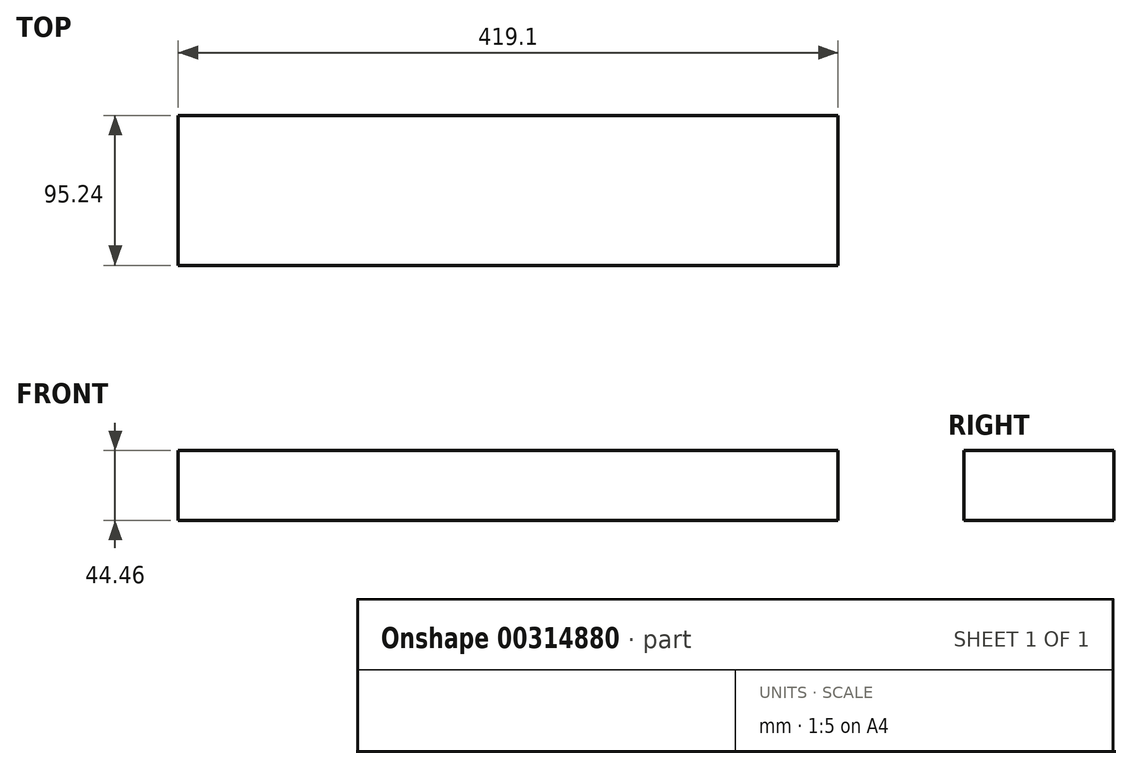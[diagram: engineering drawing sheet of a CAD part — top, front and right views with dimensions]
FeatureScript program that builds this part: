
annotation { "Feature Type Name" : "Feature", "Feature Type Description" : "" }
export const myFeature = defineFeature(function(context is Context, id is Id, definition is map)
    precondition{}
    {
        {
            var Q0;
            Q0=qCreatedBy(makeId("Right.planeOp"),FACE);
            var sketch = newSketch(context, id + "F0", { "sketchPlane" : qUnion([Q0])});
            skLineSegment(sketch, "E0.bottom", {"start": v(47.63, -22.22) * mm, "end": v(-47.62, -22.23) * mm});
            skLineSegment(sketch, "E0.top", {"start": v(47.63, 22.23) * mm, "end": v(-47.63, 22.22) * mm});
            skLineSegment(sketch, "E0.left", {"start": v(47.63, -22.22) * mm, "end": v(47.63, 22.23) * mm});
            skLineSegment(sketch, "E0.right", {"start": v(-47.63, -22.23) * mm, "end": v(-47.63, 22.23) * mm});
            skPoint(sketch, "E0.middle", {"position": v(0, 0) * mm});
            skSolve(sketch);
        }
        {
            var Q0;
            Q0 = qSketchRegion(id + "F0", true);
            extrude(context, id + "F1", {"entities" : qUnion([Q0]), "endBound" : BoundingType.SYMMETRIC, "depth" : 419.1 * mm, "offsetDistance" : 25.4 * mm});
        }
    });
